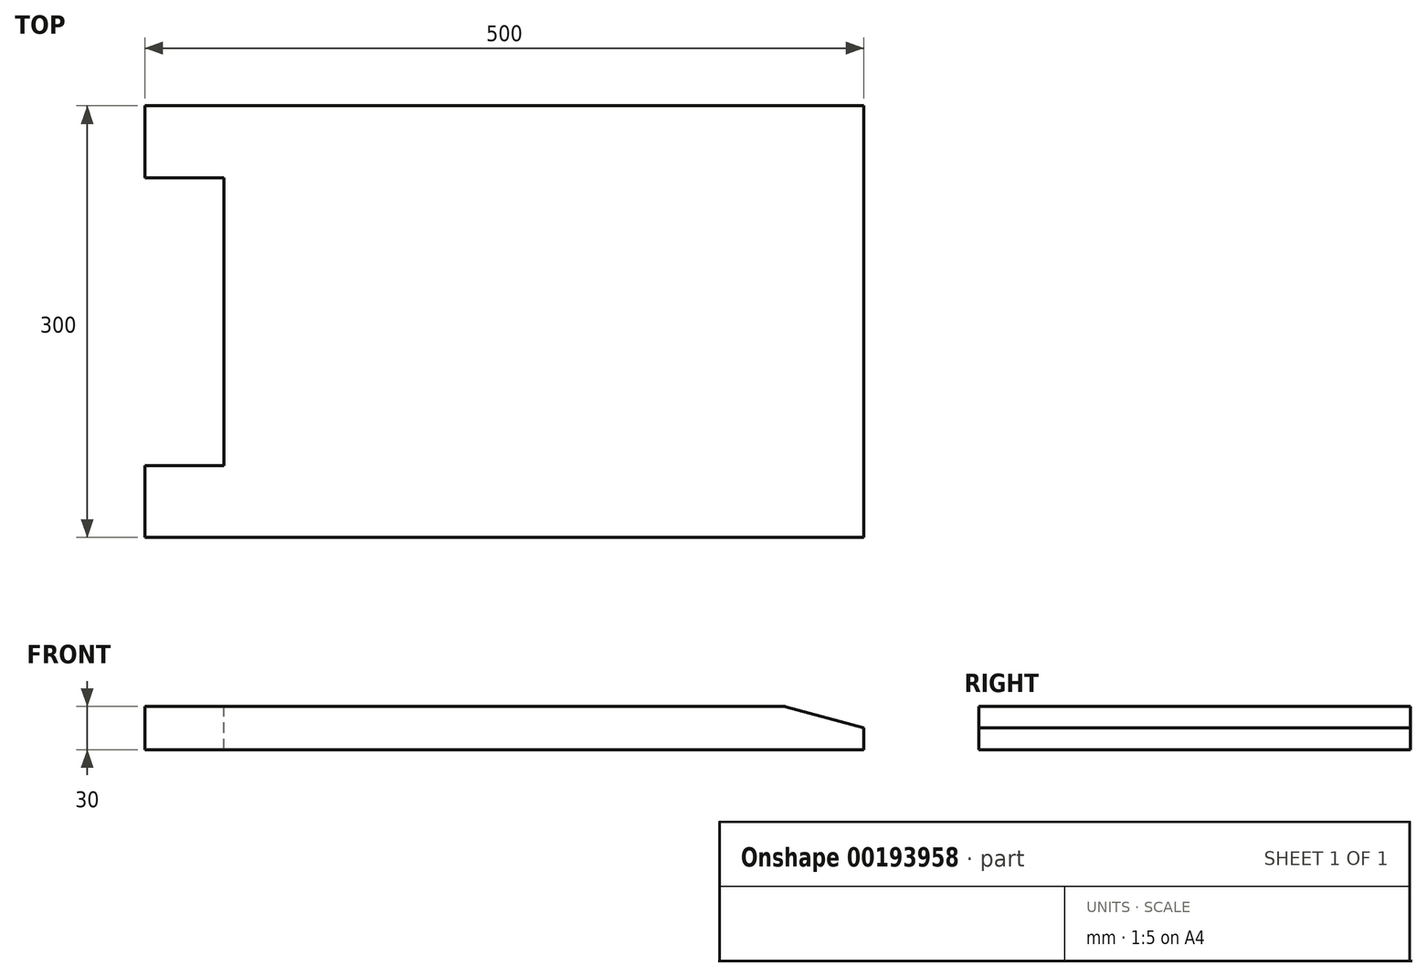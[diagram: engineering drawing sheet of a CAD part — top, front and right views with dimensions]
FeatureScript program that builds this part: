
annotation { "Feature Type Name" : "Feature", "Feature Type Description" : "" }
export const myFeature = defineFeature(function(context is Context, id is Id, definition is map)
    precondition{}
    {
        {
            var Q0;
            Q0=qCreatedBy(makeId("Top.planeOp"),FACE);
            var sketch = newSketch(context, id + "F0", { "sketchPlane" : qUnion([Q0])});
            skLineSegment(sketch, "E0.bottom", {"start": v(-250, 150) * mm, "end": v(250, 150) * mm});
            skLineSegment(sketch, "E0.top", {"start": v(-250, -150) * mm, "end": v(250, -150) * mm});
            skLineSegment(sketch, "E0.left", {"start": v(-250, 150) * mm, "end": v(-250, -150) * mm});
            skLineSegment(sketch, "E0.right", {"start": v(250, 150) * mm, "end": v(250, 100) * mm});
            skLineSegment(sketch, "E1.bottom", {"start": v(250, 100) * mm, "end": v(195, 100) * mm});
            skLineSegment(sketch, "E1.top", {"start": v(250, -100) * mm, "end": v(195, -100) * mm});
            skLineSegment(sketch, "E1.left", {"start": v(250, 100) * mm, "end": v(250, -100) * mm});
            skLineSegment(sketch, "E1.right", {"start": v(195, 100) * mm, "end": v(195, -100) * mm});
            skLineSegment(sketch, "E2", {"start": v(250, -100) * mm, "end": v(250, -150) * mm});
            skLineSegment(sketch, "E3", {"start": v(0, 150) * mm, "end": v(0, -150) * mm, "construction": true});
            skLineSegment(sketch, "E4.MirrorCS", {"start": v(-250, 100) * mm, "end": v(-195, 100) * mm});
            skLineSegment(sketch, "E5.MirrorCS", {"start": v(-195, 100) * mm, "end": v(-195, -100) * mm});
            skLineSegment(sketch, "E6.MirrorCS", {"start": v(-250, -100) * mm, "end": v(-195, -100) * mm});
            skLineSegment(sketch, "E7", {"start": v(-250, 0) * mm, "end": v(0, 0) * mm, "construction": true});
            skSolve(sketch);
        }
        {
            var Q0;
            Q0=qCreatedBy(makeId("Front.planeOp"),FACE);
            var sketch = newSketch(context, id + "F1", { "sketchPlane" : qUnion([Q0])});
            skLineSegment(sketch, "E8.0", {"start": v(250, 0) * mm, "end": v(195, 0) * mm});
            skLineSegment(sketch, "E9", {"start": v(250, 0) * mm, "end": v(250, -15) * mm});
            skLineSegment(sketch, "E10", {"start": v(250, -15) * mm, "end": v(195, 0) * mm});
            skSolve(sketch);
        }
        {
            var Q0;
            Q0=makeQuery(id+"F0.imprint","IMPRINT",FACE,{"disambiguationData":[TD([[makeQuery(id+"F0.imprint","IMPRINT",EDGE,{"derivedFrom":sQuery(id+"F0.wireOp",EDGE,"E0.bottom")}),-1.0]])]});
            extrude(context, id + "F2", {"entities" : qUnion([Q0]), "oppositeDirection" : true, "depth" : 30 * mm});
        }
        {
            var Q0;
            Q0=makeQuery(id+"F0.imprint","IMPRINT",FACE,{"disambiguationData":[TD([[makeQuery(id+"F0.imprint","IMPRINT",EDGE,{"derivedFrom":sQuery(id+"F0.wireOp",EDGE,"E1.bottom")}),1.0]])]});
            var Q1;
            Q1=makeQuery(id+"F2.opExtrude","CAP_VERTEX",VERTEX,{"disambiguationData":[OSD([sQuery(id+"F0.wireOp",EDGE,"E0.top"),sQuery(id+"F0.wireOp",EDGE,"E0.left")])],"isStart":false});
            extrude(context, id + "F3", {"entities" : qUnion([Q0]), "endBound" : BoundingType.UP_TO_VERTEX, "oppositeDirection" : true, "endBoundEntityVertex" : qUnion([Q1]), "depth" : 25 * mm});
        }
        {
            var Q0;
            Q0=makeQuery(id+"F1.imprint","IMPRINT",FACE,{"disambiguationData":[TD([[makeQuery(id+"F1.imprint","IMPRINT",EDGE,{"derivedFrom":sQuery(id+"F1.wireOp",EDGE,"E8.0")}),1.0]])]});
            extrude(context, id + "F4", {"entities" : qUnion([Q0]), "operationType" : NewBodyOperationType.REMOVE, "endBound" : BoundingType.THROUGH_ALL, "oppositeDirection" : true, "depth" : 25 * mm, "hasSecondDirection" : true, "secondDirectionBound" : SecondDirectionBoundingType.THROUGH_ALL, "secondDirectionOppositeDirection" : false, "secondDirectionDepth" : 25 * mm});
        }
        {
            var Q0;
            Q0=makeQuery(id+"F3.opExtrude","SWEPT_BODY",BODY,{"disambiguationData":[OSD([sQuery(id+"F0.wireOp",EDGE,"E1.bottom"),sQuery(id+"F0.wireOp",EDGE,"E1.top"),sQuery(id+"F0.wireOp",EDGE,"E1.right"),sQuery(id+"F0.wireOp",EDGE,"E1.left")])]});
            var Q1;
            Q1=makeQuery(id+"F2.opExtrude","SWEPT_BODY",BODY,{"disambiguationData":[OSD([sQuery(id+"F0.wireOp",EDGE,"E0.bottom"),sQuery(id+"F0.wireOp",EDGE,"E0.top"),sQuery(id+"F0.wireOp",EDGE,"E0.left"),sQuery(id+"F0.wireOp",EDGE,"E0.right"),sQuery(id+"F0.wireOp",EDGE,"E1.bottom"),sQuery(id+"F0.wireOp",EDGE,"E1.top"),sQuery(id+"F0.wireOp",EDGE,"E1.right"),sQuery(id+"F0.wireOp",EDGE,"E2"),sQuery(id+"F0.wireOp",EDGE,"E4.MirrorCS"),sQuery(id+"F0.wireOp",EDGE,"E5.MirrorCS"),sQuery(id+"F0.wireOp",EDGE,"E6.MirrorCS")])]});
            booleanBodies(context, id + "F5", {"operationType" : BooleanOperationType.UNION, "tools" : qUnion([Q0, Q1])});
        }
        {
            var Q0;
            Q0=makeQuery(id+"F4.boolean.opBoolean","INTERSECT",EDGE,{"derivedFrom":[makeQuery(id+"F3.opExtrude","SWEPT_FACE",FACE,{"disambiguationData":[OSD([sQuery(id+"F0.wireOp",EDGE,"E1.bottom")])]}),makeQuery(id+"F4.opExtrude","SWEPT_FACE",FACE,{"disambiguationData":[OSD([sQuery(id+"F1.wireOp",EDGE,"E10")])]})]});
            var Q1;
            Q1=makeQuery(id+"F4.boolean.opBoolean","INTERSECT",EDGE,{"derivedFrom":[makeQuery(id+"F3.opExtrude","SWEPT_FACE",FACE,{"disambiguationData":[OSD([sQuery(id+"F0.wireOp",EDGE,"E1.top")])]}),makeQuery(id+"F4.opExtrude","SWEPT_FACE",FACE,{"disambiguationData":[OSD([sQuery(id+"F1.wireOp",EDGE,"E10")])]})]});
            var Q2;
            Q2=makeQuery(id+"F4.boolean.opBoolean","COPY",EDGE,{"derivedFrom":makeQuery(id+"F4.opExtrude","SWEPT_EDGE",EDGE,{"disambiguationData":[OSD([sQuery(id+"F1.wireOp",EDGE,"E9"),sQuery(id+"F1.wireOp",EDGE,"E10")])]})});
            var Q3;
            {var subQ0=sQuery(id+"F0.wireOp",EDGE,"E1.right");Q3=makeQuery(id+"F5.opBoolean","MERGE",EDGE,{"derivedFrom":[makeQuery(id+"F2.opExtrude","CAP_EDGE",EDGE,{"disambiguationData":[OSD([subQ0])],"isStart":true}),makeQuery(id+"F4.boolean.opBoolean","MERGE",EDGE,{"derivedFrom":[makeQuery(id+"F3.opExtrude","CAP_EDGE",EDGE,{"disambiguationData":[OSD([subQ0])],"isStart":true}),makeQuery(id+"F4.opExtrude","SWEPT_EDGE",EDGE,{"disambiguationData":[OSD([sQuery(id+"F1.wireOp",EDGE,"E8.0"),sQuery(id+"F1.wireOp",EDGE,"E10")])]})]})]});}
            fillet(context, id + "F6", {"entities" : qUnion([Q0, Q1, Q2, Q3]), "radius" : 4 * mm, "tangentPropagation" : true, "allowEdgeOverflow" : false});
        }
    });
